# Revit family: Плита перекрытия
name_source: partatom
category: Обобщенные модели
revit_build: Autodesk Revit 2015 (Build: 20141119_1515(x64)
units: mm (PartAtom-declared; Revit-internal decimal feet)

## types (3) — shared parameters
Город и страна производства = Санкт-Петербург, Российская Федерация
Диаметр отверстия = 700 мм
Документ регламентирующий производство = ТУ 5855-001-23107031-2013
Изготовитель = ООО "ГИС"
Сайт изготовителя = http://gisspb.ru
Тип бетона = БСТ B20 П1 F200 W4 ГОСТ 7473-2010
Тип материалов покрытия = Полиэтилен низкого давления
Толщина футеровки = 4 мм

## per-type parameters (varying)
| type | Внешний диаметр | Внутрений диаметр по футеровке | Масса | Смещение отверстия | Толщина покрытия |
| ПП-20.2 ФУТ "ПБК ЭКОВЭЛЛ" с анкерными листами V-Lock | 2200 мм | 2192 мм | 1380.00 kg | 200 мм | 160 мм |
| ПП-15.2 ФУТ "ПБК ЭКОВЭЛЛ" с анкерными листами V-Lock | 1680 мм | 1672 мм | 690.00 kg | 400 мм | 160 мм |
| ПП-10.2 ФУТ "ПБК ЭКОВЭЛЛ" с анкерными листами V-Lock | 1160 мм | 1152 мм | 230.00 kg | 150 мм | 150 мм |

## geometry (parser evidence)
native form markers: Blend x4
no freeform markers — native parametric forms only
